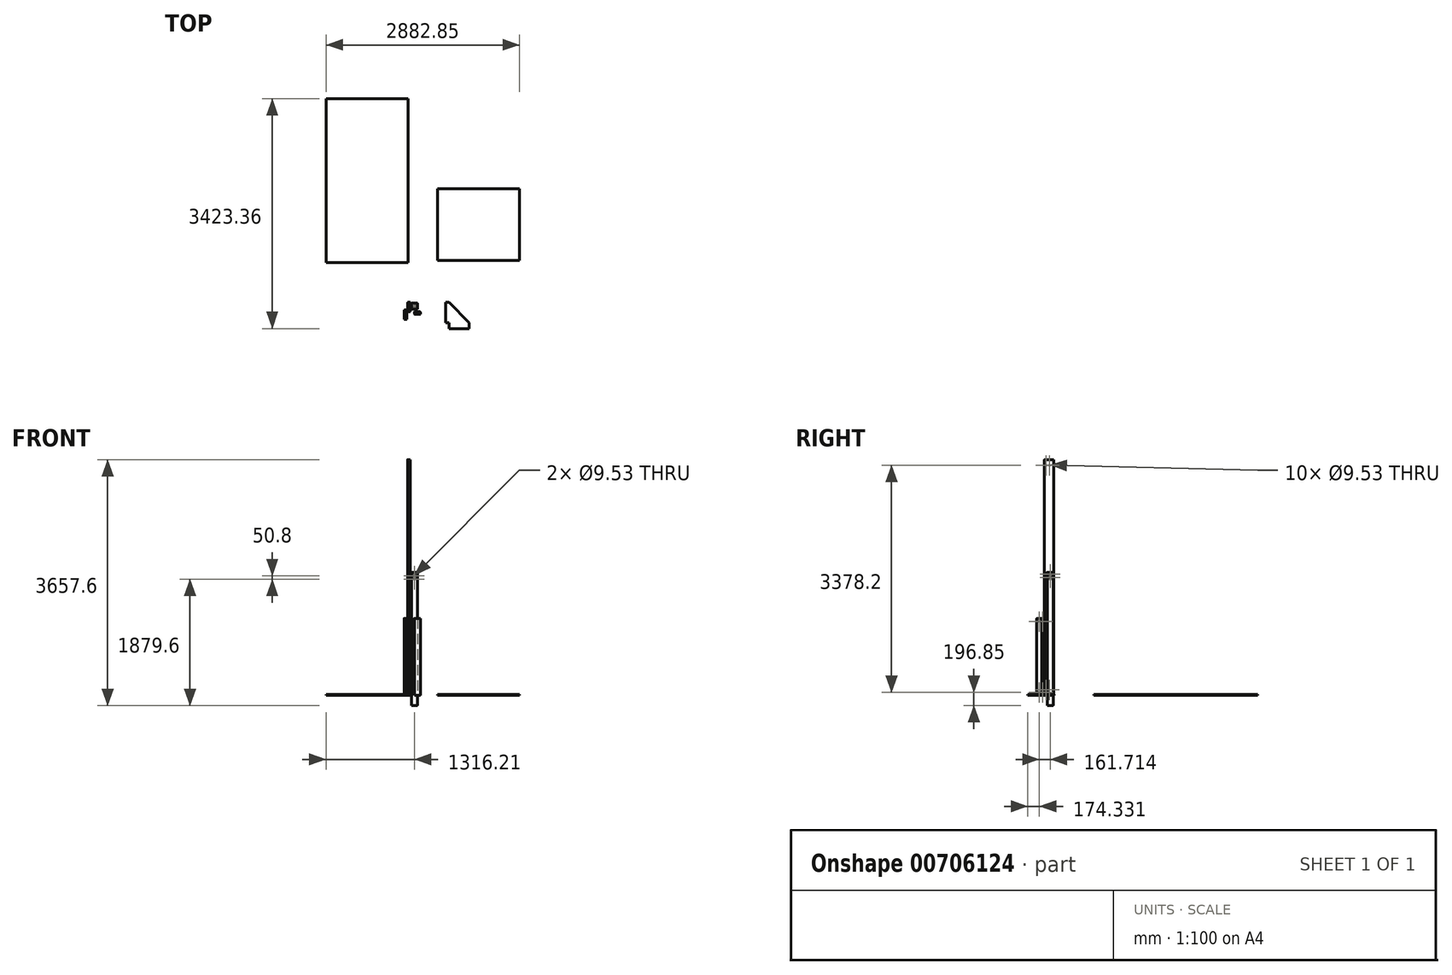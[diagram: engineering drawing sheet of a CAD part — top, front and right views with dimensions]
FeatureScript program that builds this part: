
annotation { "Feature Type Name" : "Feature", "Feature Type Description" : "" }
export const myFeature = defineFeature(function(context is Context, id is Id, definition is map)
    precondition{}
    {
        {
            var Q0;
            Q0=qCreatedBy(makeId("Top.planeOp"),FACE);
            var sketch = newSketch(context, id + "F0", { "sketchPlane" : qUnion([Q0])});
            skLineSegment(sketch, "E0.bottom", {"start": v(61.89, 0) * mm, "end": v(150.79, 0) * mm});
            skLineSegment(sketch, "E0.top", {"start": v(61.89, -38.1) * mm, "end": v(150.79, -38.1) * mm});
            skLineSegment(sketch, "E0.left", {"start": v(61.89, 0) * mm, "end": v(61.89, -38.1) * mm});
            skLineSegment(sketch, "E0.right", {"start": v(150.79, 0) * mm, "end": v(150.79, -38.1) * mm});
            skSolve(sketch);
        }
        {
            var Q0;
            Q0=makeQuery(id+"F0.imprint","IMPRINT",FACE,{"disambiguationData":[TD([[makeQuery(id+"F0.imprint","IMPRINT",EDGE,{"derivedFrom":sQuery(id+"F0.wireOp",EDGE,"E0.bottom")}),-1.0]])]});
            extrude(context, id + "F1", {"entities" : qUnion([Q0]), "depth" : 1143 * mm, "offsetDistance" : 25.4 * mm});
        }
        {
            var Q0;
            Q0=makeQuery(id+"F1.opExtrude","SWEPT_EDGE",EDGE,{"disambiguationData":[OSD([sQuery(id+"F0.wireOp",EDGE,"E0.top"),sQuery(id+"F0.wireOp",EDGE,"E0.right")])]});
            var Q1;
            Q1=makeQuery(id+"F1.opExtrude","SWEPT_EDGE",EDGE,{"disambiguationData":[OSD([sQuery(id+"F0.wireOp",EDGE,"E0.top"),sQuery(id+"F0.wireOp",EDGE,"E0.left")])]});
            var Q2;
            Q2=makeQuery(id+"F1.opExtrude","SWEPT_EDGE",EDGE,{"disambiguationData":[OSD([sQuery(id+"F0.wireOp",EDGE,"E0.bottom"),sQuery(id+"F0.wireOp",EDGE,"E0.right")])]});
            var Q3;
            Q3=makeQuery(id+"F1.opExtrude","SWEPT_EDGE",EDGE,{"disambiguationData":[OSD([sQuery(id+"F0.wireOp",EDGE,"E0.bottom"),sQuery(id+"F0.wireOp",EDGE,"E0.left")])]});
            fillet(context, id + "F2", {"entities" : qUnion([Q0, Q1, Q2, Q3]), "radius" : 5.08 * mm, "tangentPropagation" : true, "allowEdgeOverflow" : false});
        }
        {
            var Q0;
            Q0=qCreatedBy(makeId("Top.planeOp"),FACE);
            var sketch = newSketch(context, id + "F3", { "sketchPlane" : qUnion([Q0])});
            skLineSegment(sketch, "E1.bottom", {"start": v(18.61, 40.9) * mm, "end": v(107.51, 40.9) * mm});
            skLineSegment(sketch, "E1.top", {"start": v(18.61, 129.8) * mm, "end": v(107.51, 129.8) * mm});
            skLineSegment(sketch, "E1.left", {"start": v(18.61, 40.9) * mm, "end": v(18.61, 129.8) * mm});
            skLineSegment(sketch, "E1.right", {"start": v(107.51, 40.9) * mm, "end": v(107.51, 129.8) * mm});
            skSolve(sketch);
        }
        {
            var Q0;
            Q0=makeQuery(id+"F3.imprint","IMPRINT",FACE,{"disambiguationData":[TD([[makeQuery(id+"F3.imprint","IMPRINT",EDGE,{"derivedFrom":sQuery(id+"F3.wireOp",EDGE,"E1.bottom")}),1.0]])]});
            extrude(context, id + "F4", {"entities" : qUnion([Q0]), "depth" : 1828.8 * mm, "offsetDistance" : 25.4 * mm, "hasSecondDirection" : true, "secondDirectionOppositeDirection" : true, "secondDirectionDepth" : 152.4 * mm});
        }
        {
            var Q0;
            Q0=makeQuery(id+"F4.opExtrude","SWEPT_EDGE",EDGE,{"disambiguationData":[OSD([sQuery(id+"F3.wireOp",EDGE,"E1.top"),sQuery(id+"F3.wireOp",EDGE,"E1.right")])]});
            var Q1;
            Q1=makeQuery(id+"F4.opExtrude","SWEPT_EDGE",EDGE,{"disambiguationData":[OSD([sQuery(id+"F3.wireOp",EDGE,"E1.top"),sQuery(id+"F3.wireOp",EDGE,"E1.left")])]});
            var Q2;
            Q2=makeQuery(id+"F4.opExtrude","SWEPT_EDGE",EDGE,{"disambiguationData":[OSD([sQuery(id+"F3.wireOp",EDGE,"E1.bottom"),sQuery(id+"F3.wireOp",EDGE,"E1.right")])]});
            var Q3;
            Q3=makeQuery(id+"F4.opExtrude","SWEPT_EDGE",EDGE,{"disambiguationData":[OSD([sQuery(id+"F3.wireOp",EDGE,"E1.bottom"),sQuery(id+"F3.wireOp",EDGE,"E1.left")])]});
            fillet(context, id + "F5", {"entities" : qUnion([Q0, Q1, Q2, Q3]), "radius" : 5.08 * mm, "tangentPropagation" : true, "allowEdgeOverflow" : false});
        }
        {
            var Q0;
            Q0=qCreatedBy(makeId("Top.planeOp"),FACE);
            var sketch = newSketch(context, id + "F6", { "sketchPlane" : qUnion([Q0])});
            skLineSegment(sketch, "E2.bottom", {"start": v(0, 0) * mm, "end": v(-38.1, 0) * mm});
            skLineSegment(sketch, "E2.top", {"start": v(0, 139.7) * mm, "end": v(-38.1, 139.7) * mm});
            skLineSegment(sketch, "E2.left", {"start": v(0, 0) * mm, "end": v(0, 139.7) * mm});
            skLineSegment(sketch, "E2.right", {"start": v(-38.1, 0) * mm, "end": v(-38.1, 139.7) * mm});
            skSolve(sketch);
        }
        {
            var Q0;
            Q0=makeQuery(id+"F6.imprint","IMPRINT",FACE,{"disambiguationData":[TD([[makeQuery(id+"F6.imprint","IMPRINT",EDGE,{"derivedFrom":sQuery(id+"F6.wireOp",EDGE,"E2.bottom")}),-1.0]])]});
            extrude(context, id + "F7", {"entities" : qUnion([Q0]), "depth" : 3505.2 * mm, "offsetDistance" : 25.4 * mm});
        }
        {
            var Q0;
            Q0=makeQuery(id+"F7.opExtrude","SWEPT_EDGE",EDGE,{"disambiguationData":[OSD([sQuery(id+"F6.wireOp",EDGE,"E2.bottom"),sQuery(id+"F6.wireOp",EDGE,"E2.right")])]});
            var Q1;
            Q1=makeQuery(id+"F7.opExtrude","SWEPT_EDGE",EDGE,{"disambiguationData":[OSD([sQuery(id+"F6.wireOp",EDGE,"E2.bottom"),sQuery(id+"F6.wireOp",EDGE,"E2.left")])]});
            var Q2;
            Q2=makeQuery(id+"F7.opExtrude","SWEPT_EDGE",EDGE,{"disambiguationData":[OSD([sQuery(id+"F6.wireOp",EDGE,"E2.top"),sQuery(id+"F6.wireOp",EDGE,"E2.left")])]});
            var Q3;
            Q3=makeQuery(id+"F7.opExtrude","SWEPT_EDGE",EDGE,{"disambiguationData":[OSD([sQuery(id+"F6.wireOp",EDGE,"E2.top"),sQuery(id+"F6.wireOp",EDGE,"E2.right")])]});
            fillet(context, id + "F8", {"entities" : qUnion([Q0, Q1, Q2, Q3]), "radius" : 5.08 * mm, "tangentPropagation" : true, "allowEdgeOverflow" : false});
        }
        {
            var Q0;
            Q0=qCreatedBy(makeId("Top.planeOp"),FACE);
            var sketch = newSketch(context, id + "F9", { "sketchPlane" : qUnion([Q0])});
            skLineSegment(sketch, "E3.bottom", {"start": v(-88.9, 25.25) * mm, "end": v(-50.8, 25.25) * mm});
            skLineSegment(sketch, "E3.top", {"start": v(-88.9, -114.45) * mm, "end": v(-50.8, -114.45) * mm});
            skLineSegment(sketch, "E3.left", {"start": v(-88.9, 25.25) * mm, "end": v(-88.9, -114.45) * mm});
            skLineSegment(sketch, "E3.right", {"start": v(-50.8, 25.25) * mm, "end": v(-50.8, -114.45) * mm});
            skSolve(sketch);
        }
        {
            var Q0;
            Q0=makeQuery(id+"F9.imprint","IMPRINT",FACE,{"disambiguationData":[TD([[makeQuery(id+"F9.imprint","IMPRINT",EDGE,{"derivedFrom":sQuery(id+"F9.wireOp",EDGE,"E3.bottom")}),-1.0]])]});
            extrude(context, id + "F10", {"entities" : qUnion([Q0]), "depth" : 4 * 304.8 * mm - 76.2 * mm, "offsetDistance" : 25.4 * mm});
        }
        {
            var Q0;
            Q0=makeQuery(id+"F10.opExtrude","SWEPT_EDGE",EDGE,{"disambiguationData":[OSD([sQuery(id+"F9.wireOp",EDGE,"E3.top"),sQuery(id+"F9.wireOp",EDGE,"E3.left")])]});
            var Q1;
            Q1=makeQuery(id+"F10.opExtrude","SWEPT_EDGE",EDGE,{"disambiguationData":[OSD([sQuery(id+"F9.wireOp",EDGE,"E3.top"),sQuery(id+"F9.wireOp",EDGE,"E3.right")])]});
            var Q2;
            Q2=makeQuery(id+"F10.opExtrude","SWEPT_EDGE",EDGE,{"disambiguationData":[OSD([sQuery(id+"F9.wireOp",EDGE,"E3.bottom"),sQuery(id+"F9.wireOp",EDGE,"E3.left")])]});
            var Q3;
            Q3=makeQuery(id+"F10.opExtrude","SWEPT_EDGE",EDGE,{"disambiguationData":[OSD([sQuery(id+"F9.wireOp",EDGE,"E3.bottom"),sQuery(id+"F9.wireOp",EDGE,"E3.right")])]});
            fillet(context, id + "F11", {"entities" : qUnion([Q0, Q1, Q2, Q3]), "radius" : 5.08 * mm, "tangentPropagation" : true, "allowEdgeOverflow" : false});
        }
        {
            var Q0;
            Q0=qCreatedBy(makeId("Top.planeOp"),FACE);
            var sketch = newSketch(context, id + "F12", { "sketchPlane" : qUnion([Q0])});
            skLineSegment(sketch, "E4.bottom", {"start": v(-33.95, 734.28) * mm, "end": v(-1253.15, 734.28) * mm});
            skLineSegment(sketch, "E4.top", {"start": v(-33.95, 3172.68) * mm, "end": v(-1253.15, 3172.68) * mm});
            skLineSegment(sketch, "E4.left", {"start": v(-33.95, 734.28) * mm, "end": v(-33.95, 3172.68) * mm});
            skLineSegment(sketch, "E4.right", {"start": v(-1253.15, 734.28) * mm, "end": v(-1253.15, 3172.68) * mm});
            skSolve(sketch);
        }
        {
            var Q0;
            Q0=makeQuery(id+"F12.imprint","IMPRINT",FACE,{"disambiguationData":[TD([[makeQuery(id+"F12.imprint","IMPRINT",EDGE,{"derivedFrom":sQuery(id+"F12.wireOp",EDGE,"E4.bottom")}),-1.0]])]});
            extrude(context, id + "F13", {"entities" : qUnion([Q0]), "depth" : 9.52 * mm, "offsetDistance" : 25.4 * mm});
        }
        {
            var Q0;
            Q0=qCreatedBy(makeId("Top.planeOp"),FACE);
            var sketch = newSketch(context, id + "F14", { "sketchPlane" : qUnion([Q0])});
            skLineSegment(sketch, "E5.bottom", {"start": v(410.5, 766.69) * mm, "end": v(1629.7, 766.69) * mm});
            skLineSegment(sketch, "E5.top", {"start": v(410.5, 1833.49) * mm, "end": v(1629.7, 1833.49) * mm});
            skLineSegment(sketch, "E5.left", {"start": v(410.5, 766.69) * mm, "end": v(410.5, 1833.49) * mm});
            skLineSegment(sketch, "E5.right", {"start": v(1629.7, 766.69) * mm, "end": v(1629.7, 1833.49) * mm});
            skSolve(sketch);
        }
        {
            var Q0;
            Q0=makeQuery(id+"F14.imprint","IMPRINT",FACE,{"disambiguationData":[TD([[makeQuery(id+"F14.imprint","IMPRINT",EDGE,{"derivedFrom":sQuery(id+"F14.wireOp",EDGE,"E5.bottom")}),1.0]])]});
            extrude(context, id + "F15", {"entities" : qUnion([Q0]), "depth" : 9.52 * mm, "offsetDistance" : 25.4 * mm});
        }
        {
            var Q0;
            Q0=makeQuery(id+"F4.opExtrude","SWEPT_FACE",FACE,{"disambiguationData":[OSD([sQuery(id+"F3.wireOp",EDGE,"E1.right")])]});
            var sketch = newSketch(context, id + "F16", { "sketchPlane" : qUnion([Q0])});
            skCircle(sketch, "E6", {"center": v(85.35, 1803.4) * mm, "radius": 4.76 * mm});
            skCircle(sketch, "E7", {"center": v(85.36, 1752.6) * mm, "radius": 4.76 * mm});
            skLineSegment(sketch, "E8", {"start": v(85.34, 1828.8) * mm, "end": v(85.38, 1699.26) * mm, "construction": true});
            skSolve(sketch);
        }
        {
            var Q0;
            Q0=makeQuery(id+"F16.imprint","IMPRINT",FACE,{"disambiguationData":[TD([[makeQuery(id+"F16.imprint","IMPRINT",EDGE,{"derivedFrom":sQuery(id+"F16.wireOp",EDGE,"E6")}),1.0]])]});
            var Q1;
            Q1=makeQuery(id+"F16.imprint","IMPRINT",FACE,{"disambiguationData":[TD([[makeQuery(id+"F16.imprint","IMPRINT",EDGE,{"derivedFrom":sQuery(id+"F16.wireOp",EDGE,"E7")}),1.0]])]});
            extrude(context, id + "F17", {"entities" : qUnion([Q0, Q1]), "operationType" : NewBodyOperationType.REMOVE, "endBound" : BoundingType.UP_TO_NEXT, "oppositeDirection" : true, "depth" : 25.4 * mm, "offsetDistance" : 25.4 * mm});
        }
        {
            var Q0;
            Q0=makeQuery(id+"F4.opExtrude","SWEPT_FACE",FACE,{"disambiguationData":[OSD([sQuery(id+"F3.wireOp",EDGE,"E1.bottom")])]});
            var sketch = newSketch(context, id + "F18", { "sketchPlane" : qUnion([Q0])});
            skCircle(sketch, "E9", {"center": v(63.06, 1778) * mm, "radius": 4.76 * mm});
            skCircle(sketch, "E10", {"center": v(63.06, 1727.2) * mm, "radius": 4.76 * mm});
            skLineSegment(sketch, "E11", {"start": v(63.06, 1828.8) * mm, "end": v(63.06, 1706.4) * mm, "construction": true});
            skSolve(sketch);
        }
        {
            var Q0;
            Q0=makeQuery(id+"F18.imprint","IMPRINT",FACE,{"disambiguationData":[TD([[makeQuery(id+"F18.imprint","IMPRINT",EDGE,{"derivedFrom":sQuery(id+"F18.wireOp",EDGE,"E9")}),1.0]])]});
            var Q1;
            Q1=makeQuery(id+"F18.imprint","IMPRINT",FACE,{"disambiguationData":[TD([[makeQuery(id+"F18.imprint","IMPRINT",EDGE,{"derivedFrom":sQuery(id+"F18.wireOp",EDGE,"E10")}),1.0]])]});
            extrude(context, id + "F19", {"entities" : qUnion([Q0, Q1]), "operationType" : NewBodyOperationType.REMOVE, "endBound" : BoundingType.UP_TO_NEXT, "oppositeDirection" : true, "depth" : 25.4 * mm, "offsetDistance" : 25.4 * mm});
        }
        {
            var Q0;
            Q0=makeQuery(id+"F10.opExtrude","SWEPT_FACE",FACE,{"disambiguationData":[OSD([sQuery(id+"F9.wireOp",EDGE,"E3.left")])]});
            var sketch = newSketch(context, id + "F20", { "sketchPlane" : qUnion([Q0])});
            skCircle(sketch, "E12", {"center": v(25.55, 44.45) * mm, "radius": 4.76 * mm});
            skCircle(sketch, "E13", {"center": v(76.35, 44.45) * mm, "radius": 4.76 * mm});
            skCircle(sketch, "E14", {"center": v(25.55, 1098.55) * mm, "radius": 4.76 * mm});
            skCircle(sketch, "E15", {"center": v(76.35, 1098.55) * mm, "radius": 4.76 * mm});
            skSolve(sketch);
        }
        {
            var Q0;
            Q0=makeQuery(id+"F20.imprint","IMPRINT",FACE,{"disambiguationData":[TD([[makeQuery(id+"F20.imprint","IMPRINT",EDGE,{"derivedFrom":sQuery(id+"F20.wireOp",EDGE,"E14")}),1.0]])]});
            var Q1;
            Q1=makeQuery(id+"F20.imprint","IMPRINT",FACE,{"disambiguationData":[TD([[makeQuery(id+"F20.imprint","IMPRINT",EDGE,{"derivedFrom":sQuery(id+"F20.wireOp",EDGE,"E15")}),1.0]])]});
            var Q2;
            Q2=makeQuery(id+"F20.imprint","IMPRINT",FACE,{"disambiguationData":[TD([[makeQuery(id+"F20.imprint","IMPRINT",EDGE,{"derivedFrom":sQuery(id+"F20.wireOp",EDGE,"E12")}),1.0]])]});
            var Q3;
            Q3=makeQuery(id+"F20.imprint","IMPRINT",FACE,{"disambiguationData":[TD([[makeQuery(id+"F20.imprint","IMPRINT",EDGE,{"derivedFrom":sQuery(id+"F20.wireOp",EDGE,"E13")}),1.0]])]});
            extrude(context, id + "F21", {"entities" : qUnion([Q0, Q1, Q2, Q3]), "operationType" : NewBodyOperationType.REMOVE, "endBound" : BoundingType.UP_TO_NEXT, "oppositeDirection" : true, "depth" : 25.4 * mm, "offsetDistance" : 25.4 * mm});
        }
        {
            var Q0;
            Q0=makeQuery(id+"F7.opExtrude","SWEPT_FACE",FACE,{"disambiguationData":[OSD([sQuery(id+"F6.wireOp",EDGE,"E2.right")])]});
            var sketch = newSketch(context, id + "F22", { "sketchPlane" : qUnion([Q0])});
            skCircle(sketch, "E16", {"center": v(-76.2, 3422.65) * mm, "radius": 4.76 * mm});
            skCircle(sketch, "E17", {"center": v(-25.4, 3422.65) * mm, "radius": 4.76 * mm});
            skCircle(sketch, "E18", {"center": v(-76.2, 82.55) * mm, "radius": 4.76 * mm});
            skCircle(sketch, "E19", {"center": v(-25.4, 82.55) * mm, "radius": 4.76 * mm});
            skSolve(sketch);
        }
        {
            var Q0;
            Q0=makeQuery(id+"F22.imprint","IMPRINT",FACE,{"disambiguationData":[TD([[makeQuery(id+"F22.imprint","IMPRINT",EDGE,{"derivedFrom":sQuery(id+"F22.wireOp",EDGE,"E18")}),1.0]])]});
            var Q1;
            Q1=makeQuery(id+"F22.imprint","IMPRINT",FACE,{"disambiguationData":[TD([[makeQuery(id+"F22.imprint","IMPRINT",EDGE,{"derivedFrom":sQuery(id+"F22.wireOp",EDGE,"E19")}),1.0]])]});
            var Q2;
            Q2=makeQuery(id+"F22.imprint","IMPRINT",FACE,{"disambiguationData":[TD([[makeQuery(id+"F22.imprint","IMPRINT",EDGE,{"derivedFrom":sQuery(id+"F22.wireOp",EDGE,"E17")}),1.0]])]});
            var Q3;
            Q3=makeQuery(id+"F22.imprint","IMPRINT",FACE,{"disambiguationData":[TD([[makeQuery(id+"F22.imprint","IMPRINT",EDGE,{"derivedFrom":sQuery(id+"F22.wireOp",EDGE,"E16")}),1.0]])]});
            extrude(context, id + "F23", {"entities" : qUnion([Q0, Q1, Q2, Q3]), "operationType" : NewBodyOperationType.REMOVE, "endBound" : BoundingType.UP_TO_NEXT, "oppositeDirection" : true, "depth" : 25.4 * mm, "offsetDistance" : 25.4 * mm});
        }
        {
            var Q0;
            Q0=qCreatedBy(makeId("Top.planeOp"),FACE);
            var sketch = newSketch(context, id + "F24", { "sketchPlane" : qUnion([Q0])});
            skLineSegment(sketch, "E20.bottom", {"start": v(524.85, 143.02) * mm, "end": v(575.65, 143.02) * mm});
            skLineSegment(sketch, "E20.top", {"start": v(524.85, -161.78) * mm, "end": v(575.65, -161.78) * mm});
            skLineSegment(sketch, "E20.left", {"start": v(575.65, 143.02) * mm, "end": v(575.65, -161.78) * mm});
            skLineSegment(sketch, "E20.right", {"start": v(524.85, 143.02) * mm, "end": v(524.85, -161.78) * mm});
            skLineSegment(sketch, "E21.bottom", {"start": v(880.45, -250.68) * mm, "end": v(575.65, -250.68) * mm});
            skLineSegment(sketch, "E21.top", {"start": v(880.45, -161.78) * mm, "end": v(575.65, -161.78) * mm});
            skLineSegment(sketch, "E21.left", {"start": v(880.45, -250.68) * mm, "end": v(880.45, -161.78) * mm});
            skLineSegment(sketch, "E21.right", {"start": v(575.65, -250.68) * mm, "end": v(575.65, -161.78) * mm});
            skLineSegment(sketch, "E22", {"start": v(575.65, 143.02) * mm, "end": v(880.45, -161.78) * mm});
            skSolve(sketch);
        }
        {
            var Q0;
            Q0=makeQuery(id+"F24.imprint","IMPRINT",FACE,{"disambiguationData":[TD([[makeQuery(id+"F24.imprint","IMPRINT",EDGE,{"derivedFrom":sQuery(id+"F24.wireOp",EDGE,"E21.bottom")}),-1.0]])]});
            var Q1;
            Q1=makeQuery(id+"F24.imprint","IMPRINT",FACE,{"disambiguationData":[TD([[makeQuery(id+"F24.imprint","IMPRINT",EDGE,{"derivedFrom":sQuery(id+"F24.wireOp",EDGE,"E20.left")}),1.0]])]});
            var Q2;
            Q2=makeQuery(id+"F24.imprint","IMPRINT",FACE,{"disambiguationData":[TD([[makeQuery(id+"F24.imprint","IMPRINT",EDGE,{"derivedFrom":sQuery(id+"F24.wireOp",EDGE,"E20.bottom")}),-1.0]])]});
            extrude(context, id + "F25", {"entities" : qUnion([Q0, Q1, Q2]), "depth" : 9.52 * mm, "offsetDistance" : 25.4 * mm});
        }
    });
